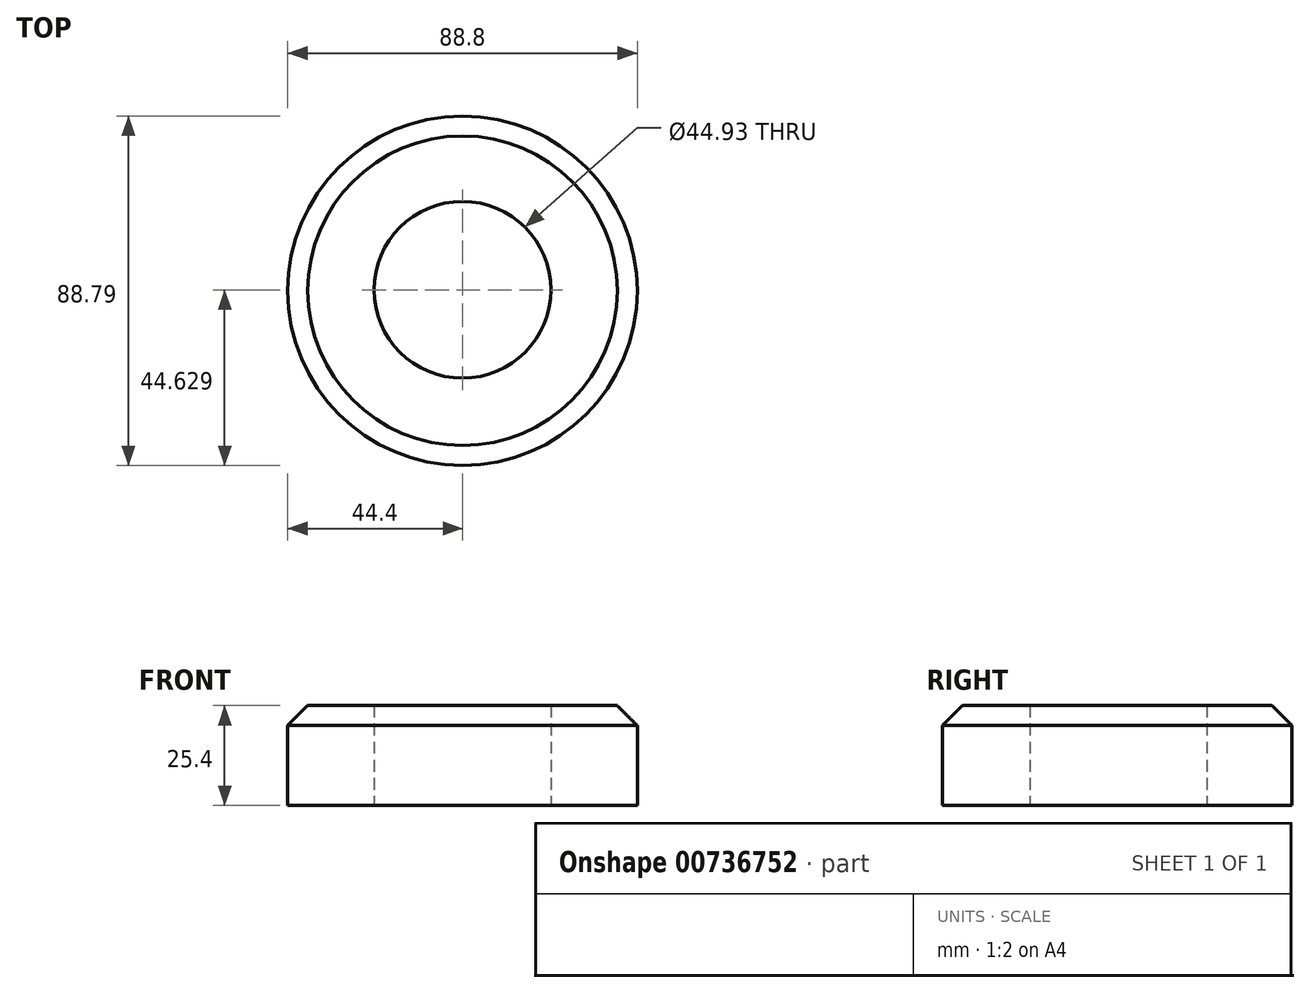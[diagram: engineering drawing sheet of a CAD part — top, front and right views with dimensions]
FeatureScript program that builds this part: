
annotation { "Feature Type Name" : "Feature", "Feature Type Description" : "" }
export const myFeature = defineFeature(function(context is Context, id is Id, definition is map)
    precondition{}
    {
        {
            var Q0;
            Q0=qCreatedBy(makeId("Top.planeOp"),FACE);
            var sketch = newSketch(context, id + "F0", { "sketchPlane" : qUnion([Q0])});
            skCircle(sketch, "E0", {"center": v(0, -24.4) * mm, "radius": 44.4 * mm});
            skSolve(sketch);
        }
        {
            var Q0;
            Q0 = qSketchRegion(id + "F0", true);
            extrude(context, id + "F1", {"entities" : qUnion([Q0]), "depth" : 25.4 * mm, "offsetDistance" : 25.4 * mm});
        }
        {
            var Q0;
            Q0=makeQuery(id+"F1.opExtrude","CAP_FACE",FACE,{"disambiguationData":[OSD([sQuery(id+"F0.wireOp",EDGE,"E0")])],"isStart":false});
            chamfer(context, id + "F2", {"entities" : qUnion([Q0]), "width" : 5.08 * mm, "tangentPropagation" : true});
        }
        {
            var Q0;
            Q0=qCreatedBy(makeId("Top.planeOp"),FACE);
            var sketch = newSketch(context, id + "F3", { "sketchPlane" : qUnion([Q0])});
            skCircle(sketch, "E1", {"center": v(0, -24.16) * mm, "radius": 22.47 * mm});
            skSolve(sketch);
        }
        {
            var Q0;
            Q0 = qSketchRegion(id + "F3", true);
            extrude(context, id + "F4", {"entities" : qUnion([Q0]), "operationType" : NewBodyOperationType.REMOVE, "endBound" : BoundingType.THROUGH_ALL, "depth" : 25.4 * mm, "offsetDistance" : 25.4 * mm});
        }
    });
